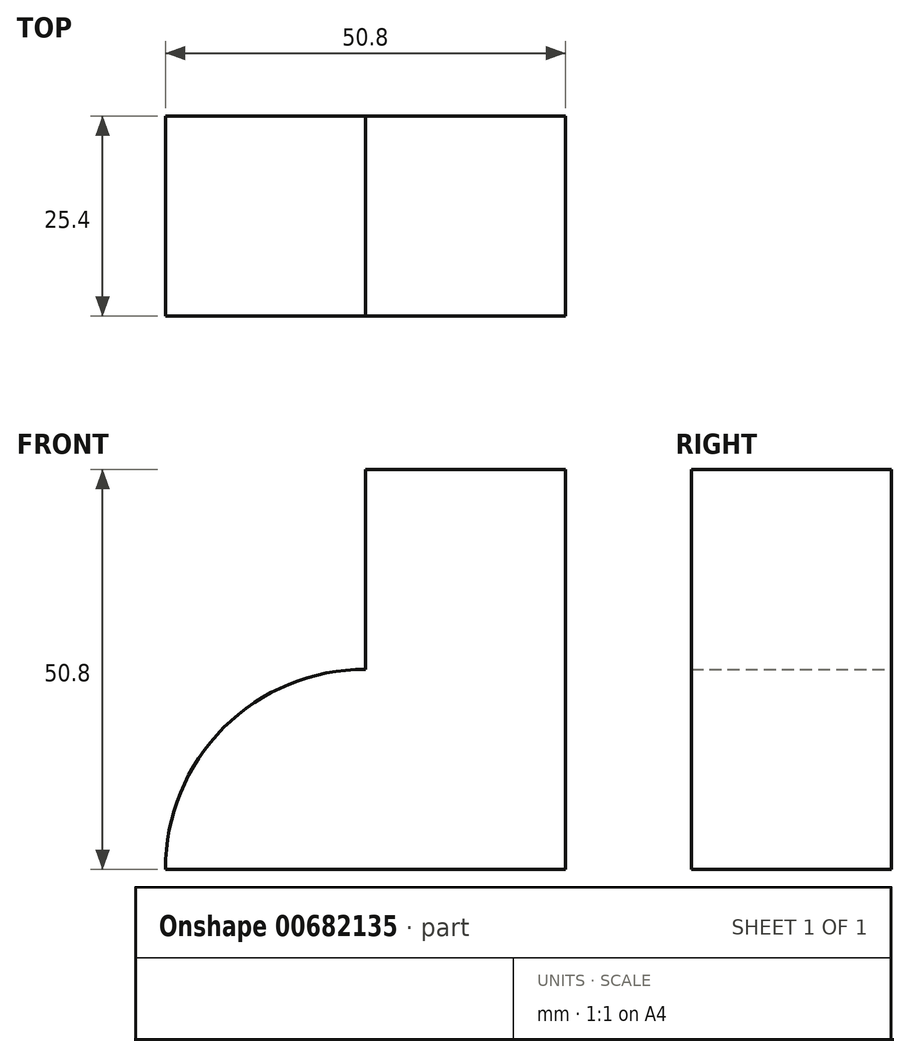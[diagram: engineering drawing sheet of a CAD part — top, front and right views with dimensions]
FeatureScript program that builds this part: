
annotation { "Feature Type Name" : "Feature", "Feature Type Description" : "" }
export const myFeature = defineFeature(function(context is Context, id is Id, definition is map)
    precondition{}
    {
        {
            var Q0;
            Q0=qCreatedBy(makeId("Front.planeOp"),FACE);
            var sketch = newSketch(context, id + "F0", { "sketchPlane" : qUnion([Q0])});
            skLineSegment(sketch, "E0", {"start": v(-15.87, 17.6) * mm, "end": v(-15.87, 43) * mm});
            skLineSegment(sketch, "E1", {"start": v(-15.87, 43) * mm, "end": v(9.53, 43) * mm});
            skLineSegment(sketch, "E2", {"start": v(9.53, 43) * mm, "end": v(9.53, -7.8) * mm});
            skLineSegment(sketch, "E3", {"start": v(9.53, -7.8) * mm, "end": v(-41.27, -7.8) * mm});
            skArc(sketch, "E4", {"start": v(-15.87, 17.6) * mm, "mid": v(-33.88, 10.2) * mm, "end": v(-41.27, -7.8) * mm});
            skSolve(sketch);
        }
        {
            var Q0;
            Q0 = qSketchRegion(id + "F0", true);
            extrude(context, id + "F1", {"entities" : qUnion([Q0]), "depth" : 25.4 * mm, "offsetDistance" : 25.4 * mm});
        }
    });
